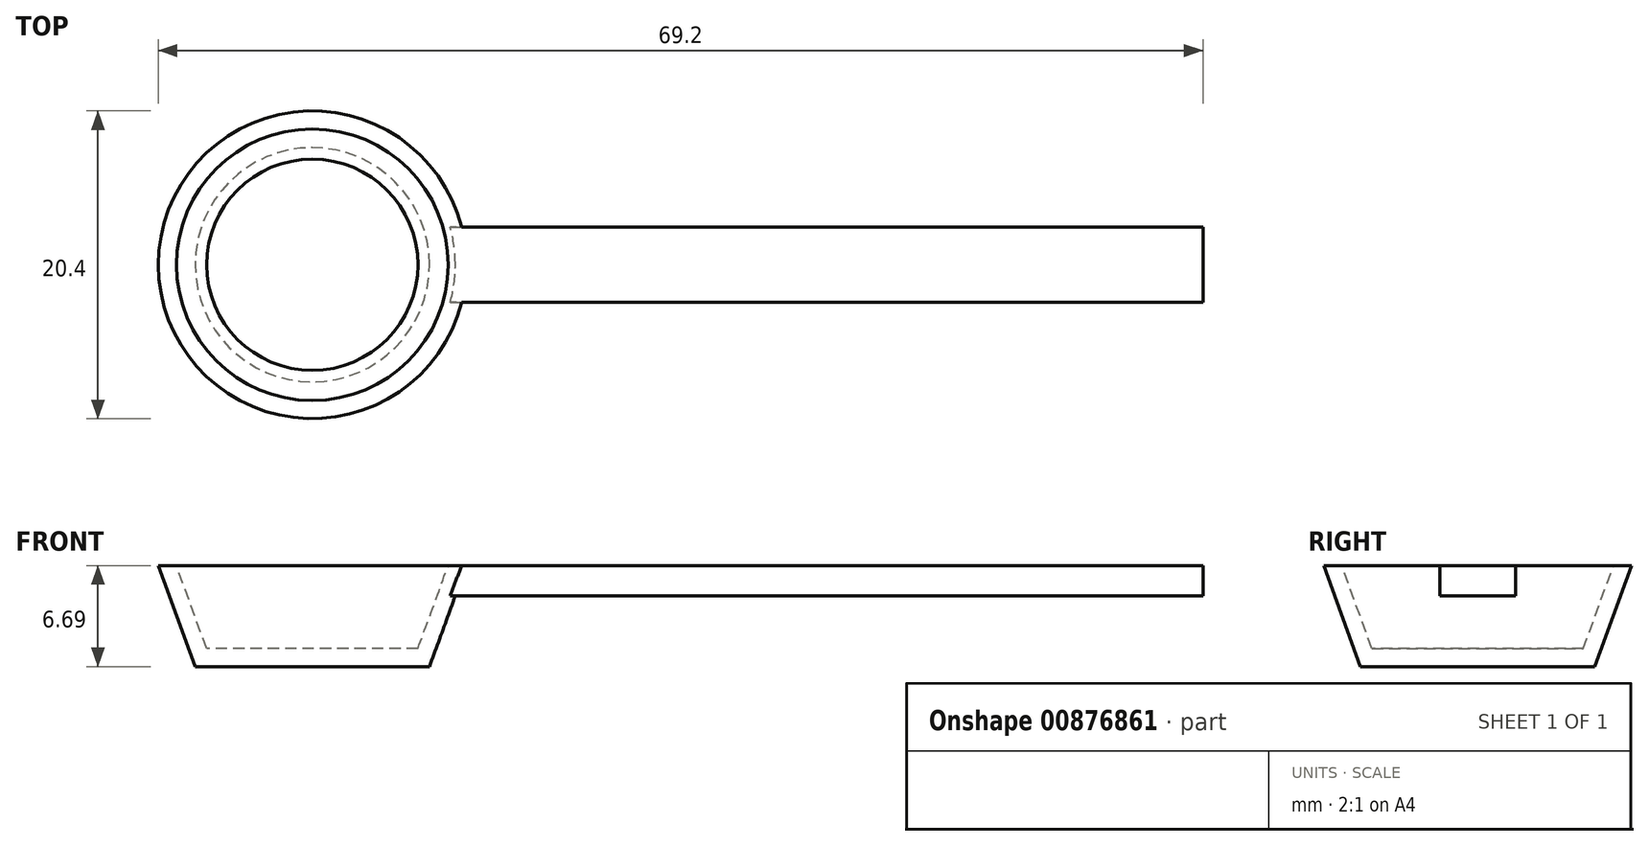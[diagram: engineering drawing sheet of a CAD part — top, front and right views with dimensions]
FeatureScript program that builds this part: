
annotation { "Feature Type Name" : "Feature", "Feature Type Description" : "" }
export const myFeature = defineFeature(function(context is Context, id is Id, definition is map)
    precondition{}
    {
        {
            var Q0;
            Q0=qCreatedBy(makeId("Front.planeOp"),FACE);
            var sketch = newSketch(context, id + "F0", { "sketchPlane" : qUnion([Q0])});
            skLineSegment(sketch, "E0.right", {"start": v(7, 1.2) * mm, "end": v(7, 0) * mm});
            skLineSegment(sketch, "E1", {"start": v(7, 0) * mm, "end": v(7.76, 0) * mm});
            skLineSegment(sketch, "E2", {"start": v(7.76, 0) * mm, "end": v(10.2, 6.7) * mm});
            skLineSegment(sketch, "E3", {"start": v(10.2, 6.7) * mm, "end": v(9, 6.7) * mm});
            skLineSegment(sketch, "E4", {"start": v(9, 6.7) * mm, "end": v(7, 1.2) * mm});
            skLineSegment(sketch, "E5", {"start": v(7, 1.2) * mm, "end": v(0, 1.2) * mm});
            skLineSegment(sketch, "E6", {"start": v(0, 1.2) * mm, "end": v(0, 0) * mm});
            skLineSegment(sketch, "E7", {"start": v(0, 0) * mm, "end": v(7, 0) * mm});
            skLineSegment(sketch, "E8", {"start": v(0, 6.43) * mm, "end": v(0, 0) * mm});
            skSolve(sketch);
        }
        {
            var Q0;
            Q0=makeQuery(id+"F0.imprint","IMPRINT",FACE,{"disambiguationData":[TD([[makeQuery(id+"F0.imprint","IMPRINT",EDGE,{"derivedFrom":sQuery(id+"F0.wireOp",EDGE,"E0.right")}),1.0]])]});
            var Q1;
            Q1=makeQuery(id+"F0.imprint","IMPRINT",FACE,{"disambiguationData":[TD([[makeQuery(id+"F0.imprint","IMPRINT",EDGE,{"derivedFrom":sQuery(id+"F0.wireOp",EDGE,"E0.right")}),-1.0]])]});
            var Q2;
            Q2=sQuery(id+"F0.wireOp",EDGE,"E8");
            revolve(context, id + "F1", {"surfaceOperationType" : NewSurfaceOperationType.NEW, "entities" : qUnion([Q0, Q1]), "axis" : qUnion([Q2]), "revolveType" : RevolveType.FULL});
        }
        {
            var Q0;
            Q0=qCreatedBy(makeId("Front.planeOp"),FACE);
            var sketch = newSketch(context, id + "F2", { "sketchPlane" : qUnion([Q0])});
            skLineSegment(sketch, "E9", {"start": v(9, 6.7) * mm, "end": v(59, 6.7) * mm});
            skLineSegment(sketch, "E10", {"start": v(59, 6.7) * mm, "end": v(59, 4.7) * mm});
            skLineSegment(sketch, "E11", {"start": v(59, 4.7) * mm, "end": v(9, 4.7) * mm});
            skLineSegment(sketch, "E12", {"start": v(9, 6.7) * mm, "end": v(9, 4.7) * mm});
            skSolve(sketch);
        }
        {
            var Q0;
            Q0 = qSketchRegion(id + "F2", true);
            extrude(context, id + "F3", {"entities" : qUnion([Q0]), "operationType" : NewBodyOperationType.ADD, "endBound" : BoundingType.SYMMETRIC, "depth" : 5 * mm, "offsetDistance" : 25 * mm});
        }
    });
